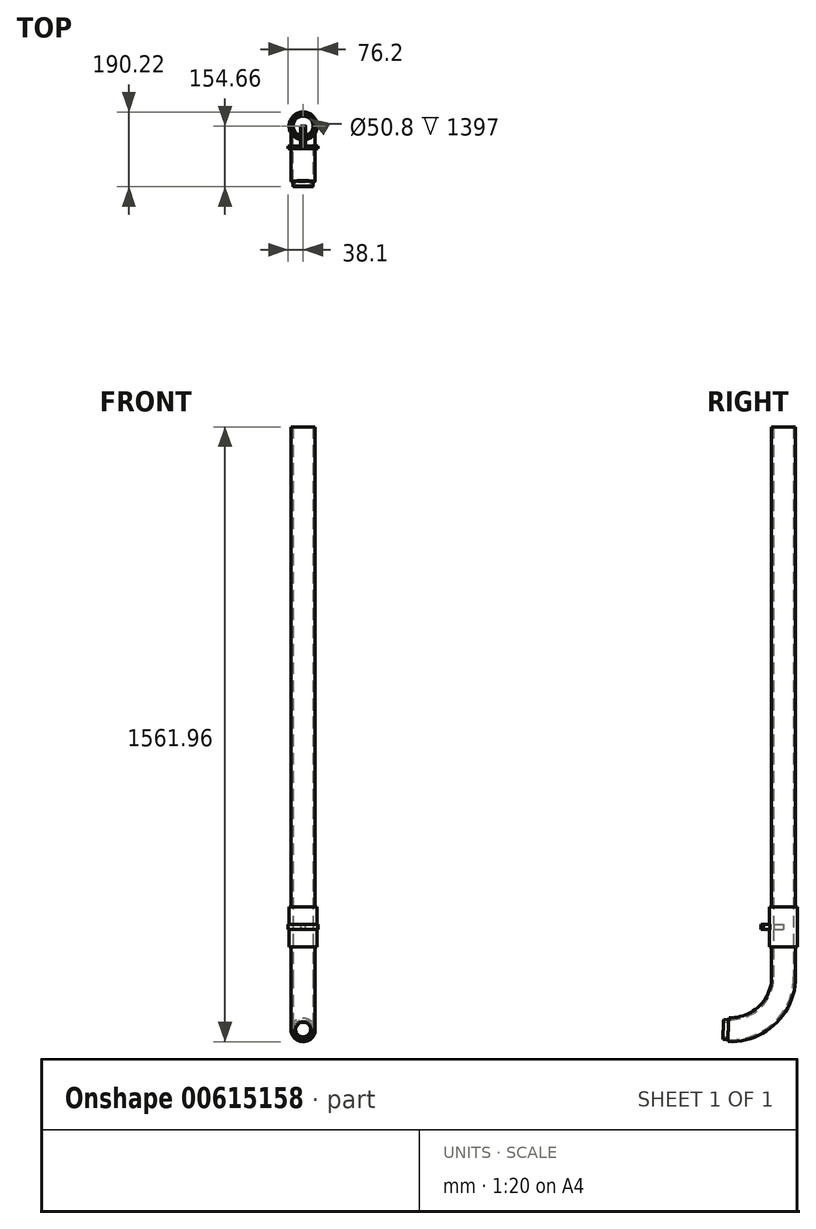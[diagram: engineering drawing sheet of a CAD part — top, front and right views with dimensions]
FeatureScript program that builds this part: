
annotation { "Feature Type Name" : "Feature", "Feature Type Description" : "" }
export const myFeature = defineFeature(function(context is Context, id is Id, definition is map)
    precondition{}
    {
        {
            var Q0;
            Q0=qCreatedBy(makeId("Top.planeOp"),FACE);
            var sketch = newSketch(context, id + "F0", { "sketchPlane" : qUnion([Q0])});
            skCircle(sketch, "E0", {"center": v(0, 0) * mm, "radius": 25.4 * mm});
            skCircle(sketch, "E1", {"center": v(0, 0) * mm, "radius": 30.48 * mm});
            skSolve(sketch);
        }
        {
            var Q0;
            Q0 = qSketchRegion(id + "F0", true);
            extrude(context, id + "F1", {"entities" : qUnion([Q0]), "depth" : 1219.2 * mm, "offsetDistance" : 25.4 * mm});
        }
        {
            var Q0;
            Q0=makeQuery(id+"F1.opExtrude","CAP_FACE",FACE,{"disambiguationData":[OSD([sQuery(id+"F0.wireOp",EDGE,"E0"),sQuery(id+"F0.wireOp",EDGE,"E1")])],"isStart":true});
            var sketch = newSketch(context, id + "F2", { "sketchPlane" : qUnion([Q0])});
            skCircle(sketch, "E2", {"center": v(0, 0) * mm, "radius": 35.56 * mm});
            skCircle(sketch, "E3", {"center": v(0, 0) * mm, "radius": 25.4 * mm});
            skSolve(sketch);
        }
        {
            var Q0;
            Q0 = qSketchRegion(id + "F2", true);
            extrude(context, id + "F3", {"entities" : qUnion([Q0]), "operationType" : NewBodyOperationType.ADD, "depth" : 101.6 * mm, "offsetDistance" : 25.4 * mm});
        }
        {
            var Q0;
            Q0=qCreatedBy(makeId("Front.planeOp"),FACE);
            var sketch = newSketch(context, id + "F4", { "sketchPlane" : qUnion([Q0])});
            skLineSegment(sketch, "E4", {"start": v(0, 0) * mm, "end": v(0, -50.8) * mm});
            skCircle(sketch, "E5", {"center": v(0, -50.8) * mm, "radius": 6.35 * mm});
            skSolve(sketch);
        }
        {
            var Q0;
            Q0 = qSketchRegion(id + "F4", true);
            extrude(context, id + "F5", {"entities" : qUnion([Q0]), "operationType" : NewBodyOperationType.ADD, "depth" : 50.8 * mm, "offsetDistance" : 25.4 * mm});
        }
        {
            var Q0;
            Q0=makeQuery(id+"F5.opExtrude","CAP_FACE",FACE,{"disambiguationData":[OSD([sQuery(id+"F4.wireOp",EDGE,"E5")])],"isStart":false});
            var sketch = newSketch(context, id + "F6", { "sketchPlane" : qUnion([Q0])});
            skLineSegment(sketch, "E6.bottom", {"start": v(38.1, -44.45) * mm, "end": v(-38.1, -44.45) * mm});
            skLineSegment(sketch, "E6.top", {"start": v(38.1, -57.15) * mm, "end": v(-38.1, -57.15) * mm});
            skLineSegment(sketch, "E6.left", {"start": v(38.1, -44.45) * mm, "end": v(38.1, -57.15) * mm});
            skLineSegment(sketch, "E6.right", {"start": v(-38.1, -44.45) * mm, "end": v(-38.1, -57.15) * mm});
            skPoint(sketch, "E6.middle", {"position": v(0, -50.8) * mm});
            skSolve(sketch);
        }
        {
            var Q0;
            Q0 = qSketchRegion(id + "F6", true);
            extrude(context, id + "F7", {"entities" : qUnion([Q0]), "operationType" : NewBodyOperationType.ADD, "depth" : 6.35 * mm, "offsetDistance" : 25.4 * mm});
        }
        {
            var Q0;
            Q0=makeQuery(id+"F3.opExtrude","CAP_FACE",FACE,{"disambiguationData":[OSD([sQuery(id+"F2.wireOp",EDGE,"E2"),sQuery(id+"F2.wireOp",EDGE,"E3")])],"isStart":false});
            var sketch = newSketch(context, id + "F8", { "sketchPlane" : qUnion([Q0])});
            skCircle(sketch, "E7", {"center": v(0, 0) * mm, "radius": 25.4 * mm});
            skCircle(sketch, "E8", {"center": v(0, 0) * mm, "radius": 30.48 * mm});
            skSolve(sketch);
        }
        {
            var Q0;
            Q0 = qSketchRegion(id + "F8", true);
            extrude(context, id + "F9", {"entities" : qUnion([Q0]), "operationType" : NewBodyOperationType.ADD, "depth" : 76.2 * mm, "offsetDistance" : 25.4 * mm});
        }
        {
            var Q0;
            Q0=qCreatedBy(makeId("Right.planeOp"),FACE);
            var sketch = newSketch(context, id + "F10", { "sketchPlane" : qUnion([Q0])});
            skArc(sketch, "E9", {"start": v(-140.78, -312.13) * mm, "mid": v(-41.64, -275.1) * mm, "end": v(0, -177.8) * mm});
            skSolve(sketch);
        }
        {
            var Q0;
            Q0=makeQuery(id+"F9.opExtrude","CAP_FACE",FACE,{"disambiguationData":[OSD([sQuery(id+"F8.wireOp",EDGE,"E7"),sQuery(id+"F8.wireOp",EDGE,"E8")])],"isStart":false});
            var Q1;
            Q1=sQuery(id+"F10.wireOp",EDGE,"E9");
            sweep(context, id + "F11", {"operationType" : NewBodyOperationType.ADD, "profiles" : qUnion([Q0]), "path" : qUnion([Q1])});
        }
        {
            var Q0;
            Q0=makeQuery(id+"F11.opSweep","CAP_FACE",FACE,{"disambiguationData":[OSD([sQuery(id+"F8.wireOp",EDGE,"E7"),sQuery(id+"F8.wireOp",EDGE,"E8"),sQuery(id+"F10.wireOp",VERTEX,"E9.start")])],"isStart":false});
            var sketch = newSketch(context, id + "F12", { "sketchPlane" : qUnion([Q0])});
            skCircle(sketch, "E10", {"center": v(0, -318.39) * mm, "radius": 25.4 * mm});
            skCircle(sketch, "E11", {"center": v(0, -318.39) * mm, "radius": 19.05 * mm});
            skSolve(sketch);
        }
        {
            var Q0;
            Q0 = qSketchRegion(id + "F12", true);
            extrude(context, id + "F13", {"entities" : qUnion([Q0]), "depth" : 12.7 * mm, "offsetDistance" : 25.4 * mm});
        }
    });
